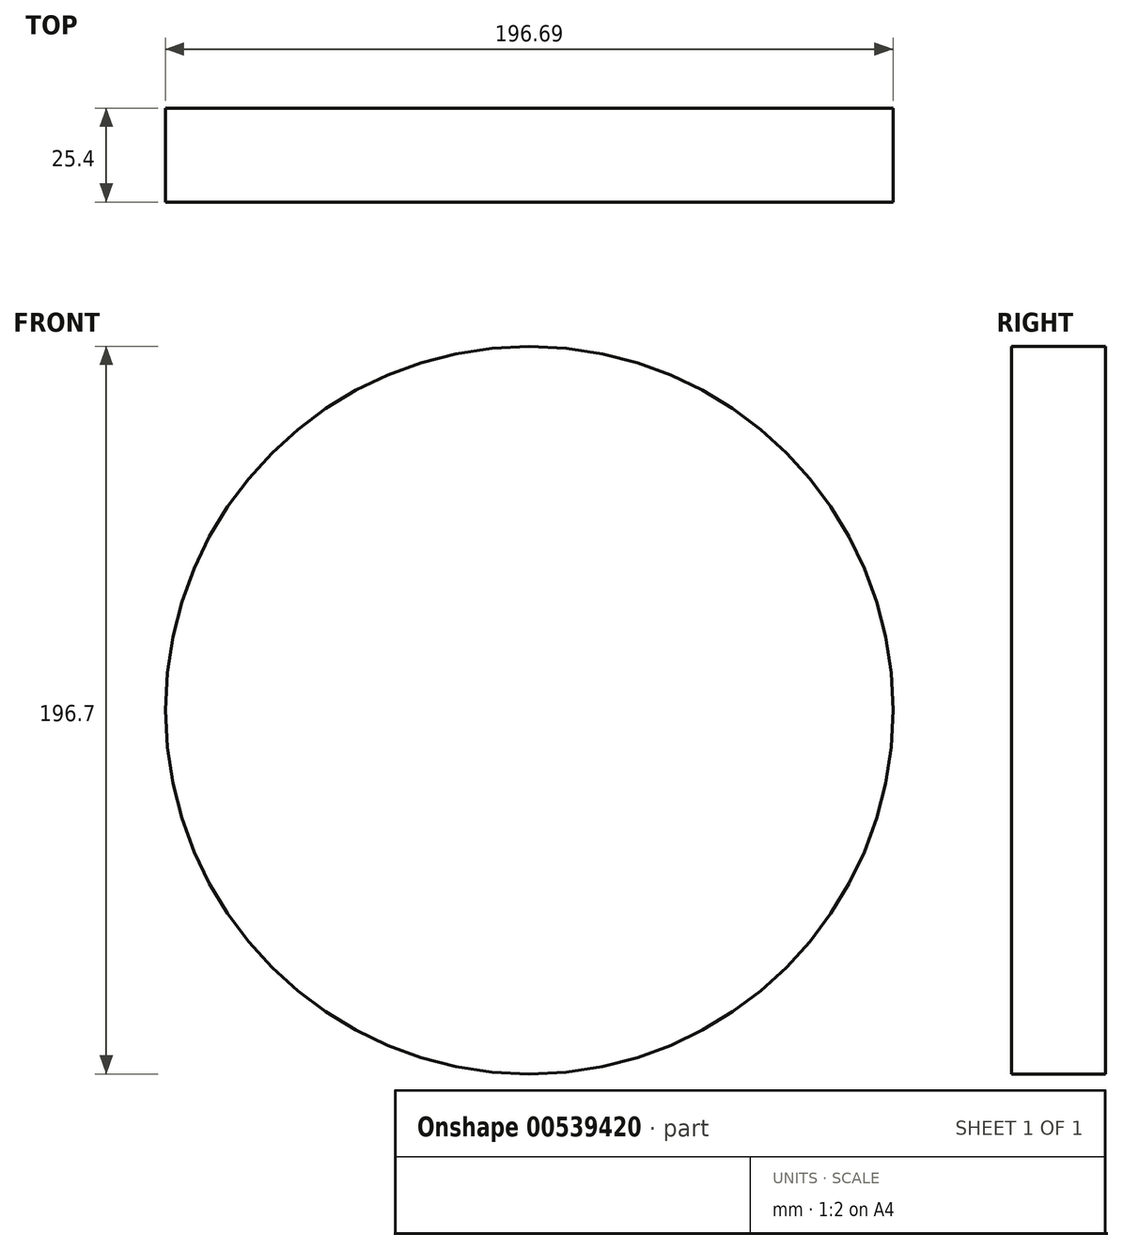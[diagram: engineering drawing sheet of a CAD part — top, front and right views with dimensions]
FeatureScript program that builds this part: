
annotation { "Feature Type Name" : "Feature", "Feature Type Description" : "" }
export const myFeature = defineFeature(function(context is Context, id is Id, definition is map)
    precondition{}
    {
        {
            var Q0;
            Q0=qCreatedBy(makeId("Front.planeOp"),FACE);
            var sketch = newSketch(context, id + "F0", { "sketchPlane" : qUnion([Q0])});
            skCircle(sketch, "E0", {"center": v(82.99, 0) * mm, "radius": 98.35 * mm});
            skSolve(sketch);
        }
        {
            var Q0;
            Q0 = qSketchRegion(id + "F0", true);
            extrude(context, id + "F1", {"entities" : qUnion([Q0]), "depth" : 25.4 * mm, "offsetDistance" : 25.4 * mm});
        }
    });
